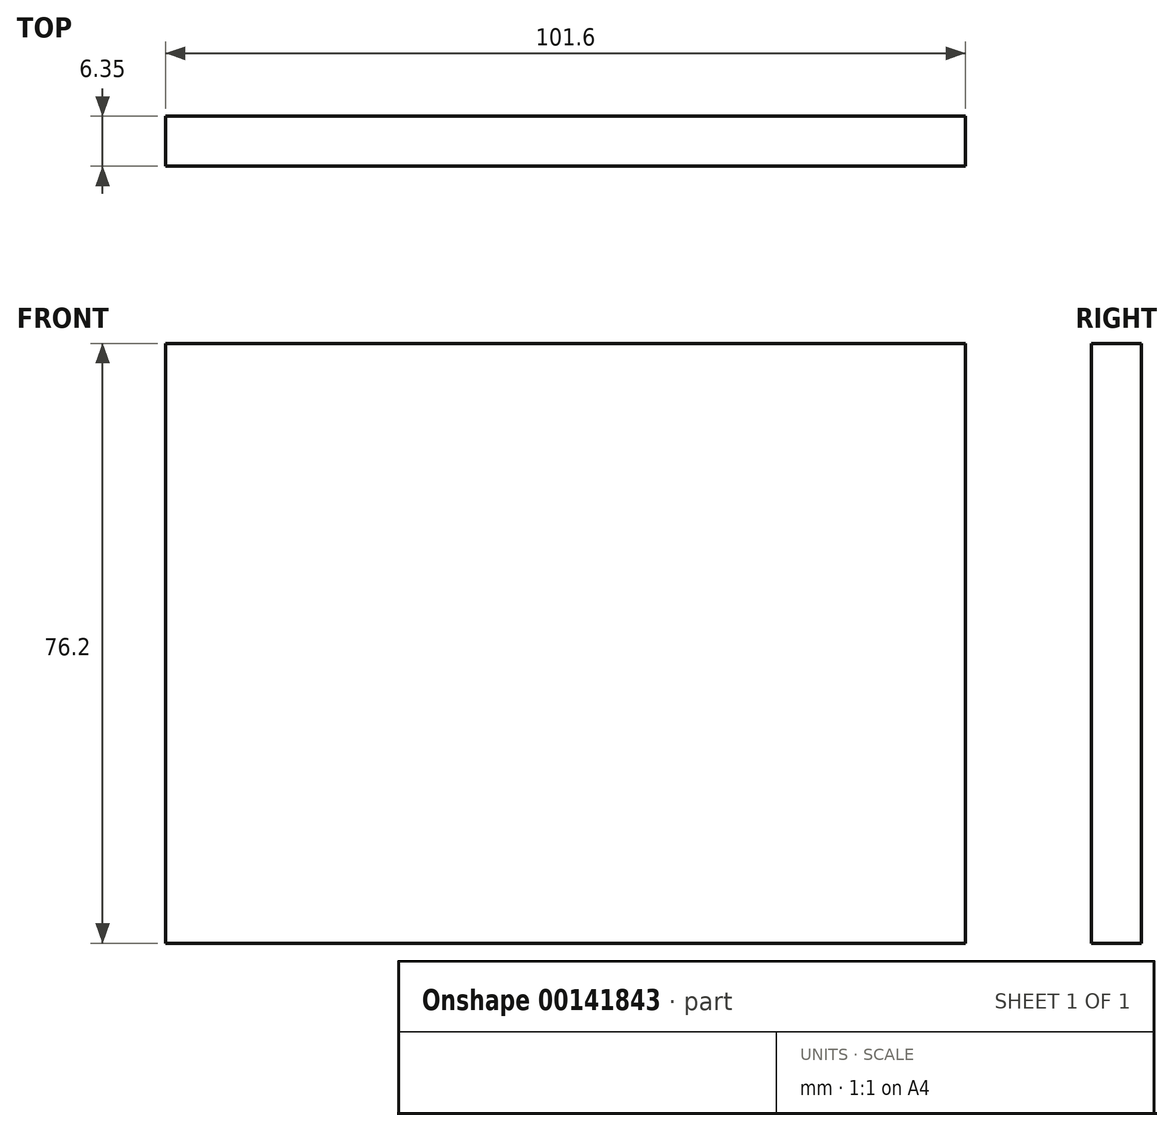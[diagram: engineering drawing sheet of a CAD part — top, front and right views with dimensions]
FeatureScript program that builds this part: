
annotation { "Feature Type Name" : "Feature", "Feature Type Description" : "" }
export const myFeature = defineFeature(function(context is Context, id is Id, definition is map)
    precondition{}
    {
        {
            var Q0;
            Q0=qCreatedBy(makeId("Front.planeOp"),FACE);
            var sketch = newSketch(context, id + "F0", { "sketchPlane" : qUnion([Q0])});
            skLineSegment(sketch, "E0.bottom", {"start": v(50.8, -38.1) * mm, "end": v(-50.8, -38.1) * mm});
            skLineSegment(sketch, "E0.top", {"start": v(50.8, 38.1) * mm, "end": v(-50.8, 38.1) * mm});
            skLineSegment(sketch, "E0.left", {"start": v(50.8, -38.1) * mm, "end": v(50.8, 38.1) * mm});
            skLineSegment(sketch, "E0.right", {"start": v(-50.8, -38.1) * mm, "end": v(-50.8, 38.1) * mm});
            skPoint(sketch, "E0.middle", {"position": v(0, 0) * mm});
            skSolve(sketch);
        }
        {
            var Q0;
            Q0=makeQuery(id+"F0.imprint","IMPRINT",FACE,{"disambiguationData":[TD([[makeQuery(id+"F0.imprint","IMPRINT",EDGE,{"derivedFrom":sQuery(id+"F0.wireOp",EDGE,"E0.bottom")}),-1.0]])]});
            extrude(context, id + "F1", {"entities" : qUnion([Q0]), "oppositeDirection" : true, "depth" : 6.35 * mm});
        }
    });
